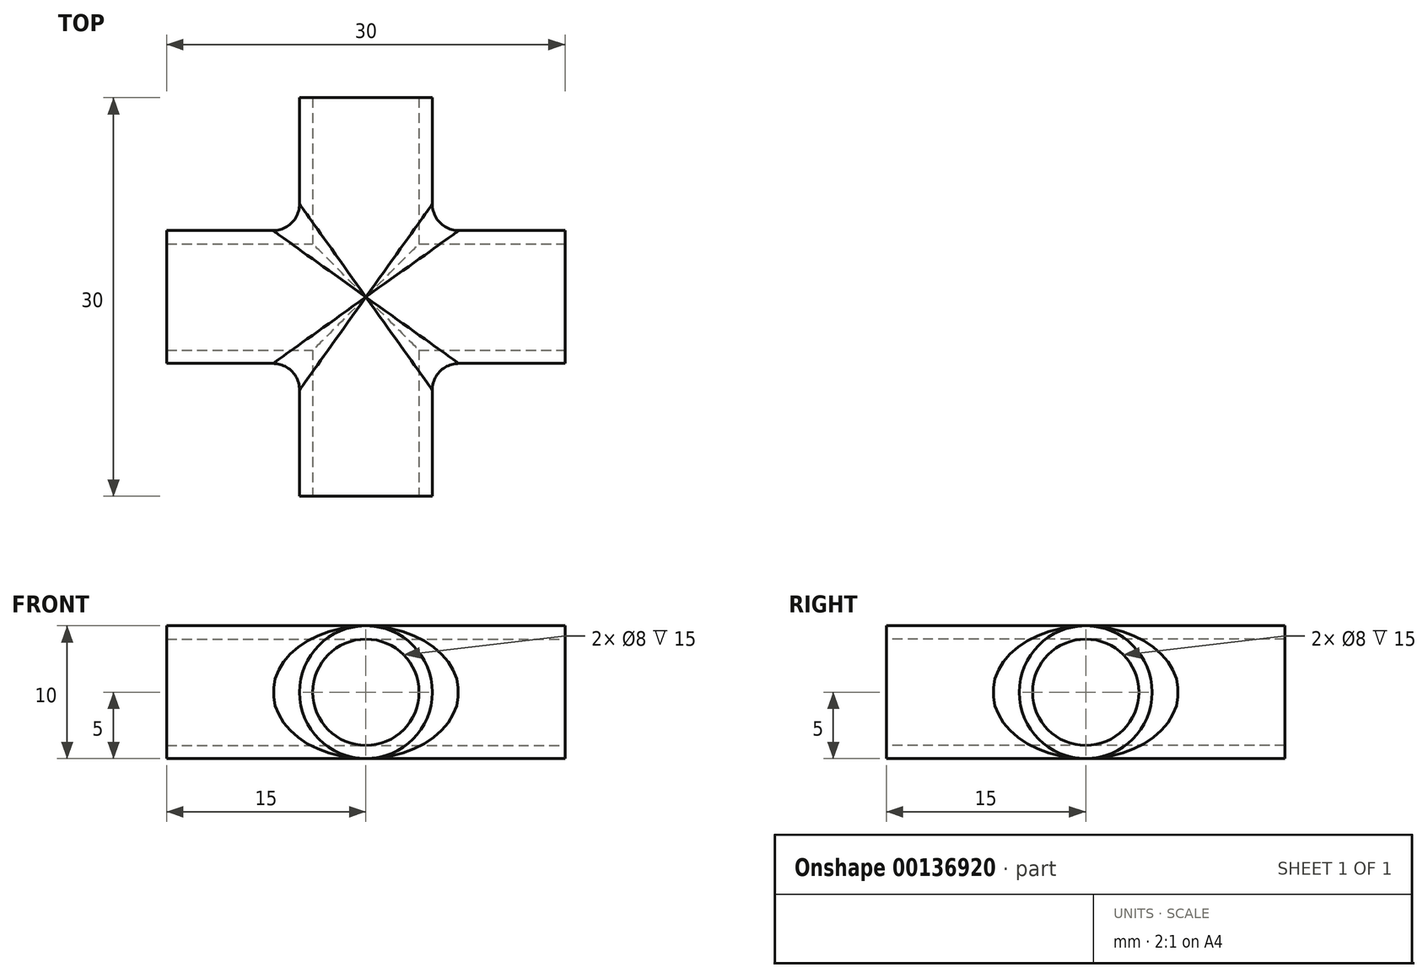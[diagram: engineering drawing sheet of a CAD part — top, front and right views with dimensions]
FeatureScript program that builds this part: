
annotation { "Feature Type Name" : "Feature", "Feature Type Description" : "" }
export const myFeature = defineFeature(function(context is Context, id is Id, definition is map)
    precondition{}
    {
        {
            var Q0;
            Q0=qCreatedBy(makeId("Front.planeOp"),FACE);
            var sketch = newSketch(context, id + "F0", { "sketchPlane" : qUnion([Q0])});
            skCircle(sketch, "E0", {"center": v(0, 0) * mm, "radius": 5 * mm});
            skSolve(sketch);
        }
        {
            var Q0;
            Q0 = qSketchRegion(id + "F0", true);
            extrude(context, id + "F1", {"entities" : qUnion([Q0]), "depth" : 15 * mm, "hasSecondDirection" : true, "secondDirectionOppositeDirection" : true, "secondDirectionDepth" : 15 * mm});
        }
        {
            var Q0;
            Q0=qCreatedBy(makeId("Right.planeOp"),FACE);
            var sketch = newSketch(context, id + "F2", { "sketchPlane" : qUnion([Q0])});
            skCircle(sketch, "E1", {"center": v(0, 0) * mm, "radius": 5 * mm});
            skSolve(sketch);
        }
        {
            var Q0;
            Q0 = qSketchRegion(id + "F2", true);
            extrude(context, id + "F3", {"entities" : qUnion([Q0]), "operationType" : NewBodyOperationType.ADD, "depth" : 15 * mm, "hasSecondDirection" : true, "secondDirectionOppositeDirection" : true, "secondDirectionDepth" : 15 * mm});
        }
        {
            var Q0;
            Q0=makeQuery(id+"F1.opExtrude","CAP_FACE",FACE,{"disambiguationData":[OSD([sQuery(id+"F0.wireOp",EDGE,"E0")])],"isStart":false});
            var sketch = newSketch(context, id + "F4", { "sketchPlane" : qUnion([Q0])});
            skCircle(sketch, "E2.0", {"center": v(0, 0) * mm, "radius": 4 * mm});
            skSolve(sketch);
        }
        {
            var Q0;
            Q0 = qSketchRegion(id + "F4", true);
            extrude(context, id + "F5", {"entities" : qUnion([Q0]), "operationType" : NewBodyOperationType.REMOVE, "endBound" : BoundingType.THROUGH_ALL, "oppositeDirection" : true, "depth" : 25 * mm});
        }
        {
            var Q0;
            Q0=makeQuery(id+"F3.opExtrude","CAP_FACE",FACE,{"disambiguationData":[OSD([sQuery(id+"F2.wireOp",EDGE,"E1")])],"isStart":false});
            var sketch = newSketch(context, id + "F6", { "sketchPlane" : qUnion([Q0])});
            skCircle(sketch, "E3.0", {"center": v(0, 0) * mm, "radius": 4 * mm});
            skSolve(sketch);
        }
        {
            var Q0;
            Q0 = qSketchRegion(id + "F6", true);
            extrude(context, id + "F7", {"entities" : qUnion([Q0]), "operationType" : NewBodyOperationType.REMOVE, "oppositeDirection" : true, "depth" : 35 * mm});
        }
        {
            var Q0;
            Q0=makeQuery(id+"F3.boolean.opBoolean","INTERSECT",EDGE,{"disambiguationData":[OD(1.0)],"derivedFrom":[makeQuery(id+"F1.opExtrude","SWEPT_FACE",FACE,{"disambiguationData":[OSD([sQuery(id+"F0.wireOp",EDGE,"E0")])]}),makeQuery(id+"F3.opExtrude","SWEPT_FACE",FACE,{"disambiguationData":[OSD([sQuery(id+"F2.wireOp",EDGE,"E1")])]})]});
            var Q1;
            Q1=makeQuery(id+"F3.boolean.opBoolean","INTERSECT",EDGE,{"disambiguationData":[OD(2.0)],"derivedFrom":[makeQuery(id+"F1.opExtrude","SWEPT_FACE",FACE,{"disambiguationData":[OSD([sQuery(id+"F0.wireOp",EDGE,"E0")])]}),makeQuery(id+"F3.opExtrude","SWEPT_FACE",FACE,{"disambiguationData":[OSD([sQuery(id+"F2.wireOp",EDGE,"E1")])]})]});
            var Q2;
            Q2=makeQuery(id+"F3.boolean.opBoolean","INTERSECT",EDGE,{"disambiguationData":[OD(0.0)],"derivedFrom":[makeQuery(id+"F1.opExtrude","SWEPT_FACE",FACE,{"disambiguationData":[OSD([sQuery(id+"F0.wireOp",EDGE,"E0")])]}),makeQuery(id+"F3.opExtrude","SWEPT_FACE",FACE,{"disambiguationData":[OSD([sQuery(id+"F2.wireOp",EDGE,"E1")])]})]});
            var Q3;
            Q3=makeQuery(id+"F3.boolean.opBoolean","INTERSECT",EDGE,{"disambiguationData":[OD(3.0)],"derivedFrom":[makeQuery(id+"F1.opExtrude","SWEPT_FACE",FACE,{"disambiguationData":[OSD([sQuery(id+"F0.wireOp",EDGE,"E0")])]}),makeQuery(id+"F3.opExtrude","SWEPT_FACE",FACE,{"disambiguationData":[OSD([sQuery(id+"F2.wireOp",EDGE,"E1")])]})]});
            fillet(context, id + "F8", {"entities" : qUnion([Q0, Q1, Q2, Q3]), "radius" : 2 * mm, "tangentPropagation" : true, "allowEdgeOverflow" : false});
        }
    });
